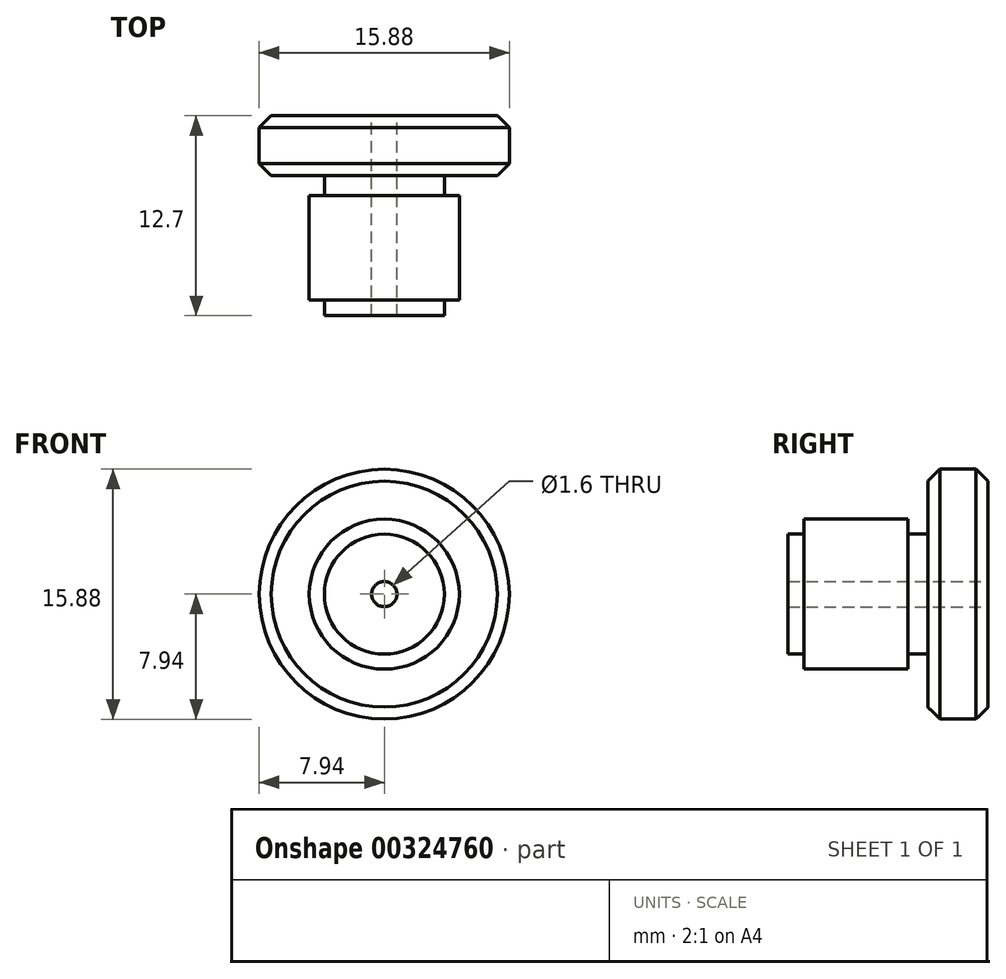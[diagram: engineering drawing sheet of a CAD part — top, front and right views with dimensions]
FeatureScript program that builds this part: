
annotation { "Feature Type Name" : "Feature", "Feature Type Description" : "" }
export const myFeature = defineFeature(function(context is Context, id is Id, definition is map)
    precondition{}
    {
        {
            var Q0;
            Q0=qCreatedBy(makeId("Front.planeOp"),FACE);
            var sketch = newSketch(context, id + "F0", { "sketchPlane" : qUnion([Q0])});
            skCircle(sketch, "E0", {"center": v(0, 0) * mm, "radius": 7.94 * mm});
            skSolve(sketch);
        }
        {
            var Q0;
            Q0=makeQuery(id+"F0.imprint","IMPRINT",FACE,{"disambiguationData":[TD([[makeQuery(id+"F0.imprint","IMPRINT",EDGE,{"derivedFrom":sQuery(id+"F0.wireOp",EDGE,"E0")}),1.0]])]});
            extrude(context, id + "F1", {"entities" : qUnion([Q0]), "depth" : 3.8 * mm, "offsetDistance" : 25.4 * mm});
        }
        {
            var Q0;
            Q0=makeQuery(id+"F1.opExtrude","CAP_FACE",FACE,{"disambiguationData":[OSD([sQuery(id+"F0.wireOp",EDGE,"E0")])],"isStart":false});
            var sketch = newSketch(context, id + "F2", { "sketchPlane" : qUnion([Q0])});
            skCircle(sketch, "E1", {"center": v(0, 0) * mm, "radius": 4.76 * mm});
            skSolve(sketch);
        }
        {
            var Q0;
            Q0=makeQuery(id+"F2.imprint","IMPRINT",FACE,{"disambiguationData":[TD([[makeQuery(id+"F2.imprint","IMPRINT",EDGE,{"derivedFrom":sQuery(id+"F2.wireOp",EDGE,"E1")}),1.0]])]});
            extrude(context, id + "F3", {"entities" : qUnion([Q0]), "operationType" : NewBodyOperationType.ADD, "depth" : 8.9 * mm, "offsetDistance" : 25.4 * mm});
        }
        {
            var Q0;
            Q0=qCreatedBy(makeId("Right.planeOp"),FACE);
            var sketch = newSketch(context, id + "F4", { "sketchPlane" : qUnion([Q0])});
            skLineSegment(sketch, "E2.bottom", {"start": v(-3.81, 3.81) * mm, "end": v(-5.08, 3.81) * mm});
            skLineSegment(sketch, "E2.top", {"start": v(-3.81, 5.97) * mm, "end": v(-5.08, 5.97) * mm});
            skLineSegment(sketch, "E2.left", {"start": v(-3.81, 3.81) * mm, "end": v(-3.81, 5.97) * mm});
            skLineSegment(sketch, "E2.right", {"start": v(-5.08, 3.81) * mm, "end": v(-5.08, 5.97) * mm});
            skSolve(sketch);
        }
        {
            var Q0;
            Q0=makeQuery(id+"F4.imprint","IMPRINT",FACE,{"disambiguationData":[TD([[makeQuery(id+"F4.imprint","IMPRINT",EDGE,{"derivedFrom":sQuery(id+"F4.wireOp",EDGE,"E2.bottom")}),-1.0]])]});
            var Q1;
            Q1=makeQuery(id+"F1.opExtrude","CAP_EDGE",EDGE,{"disambiguationData":[OSD([sQuery(id+"F0.wireOp",EDGE,"E0")])],"isStart":false});
            sweep(context, id + "F5", {"operationType" : NewBodyOperationType.REMOVE, "profiles" : qUnion([Q0]), "path" : qUnion([Q1])});
        }
        {
            var Q0;
            Q0=qCreatedBy(makeId("Right.planeOp"),FACE);
            var sketch = newSketch(context, id + "F6", { "sketchPlane" : qUnion([Q0])});
            skLineSegment(sketch, "E3.bottom", {"start": v(-13.73, 6.97) * mm, "end": v(-11.7, 6.97) * mm});
            skLineSegment(sketch, "E3.top", {"start": v(-13.73, 3.81) * mm, "end": v(-11.7, 3.81) * mm});
            skLineSegment(sketch, "E3.left", {"start": v(-13.73, 6.97) * mm, "end": v(-13.73, 3.81) * mm});
            skLineSegment(sketch, "E3.right", {"start": v(-11.7, 6.97) * mm, "end": v(-11.7, 3.81) * mm});
            skSolve(sketch);
        }
        {
            var Q0;
            Q0=makeQuery(id+"F6.imprint","IMPRINT",FACE,{"disambiguationData":[TD([[makeQuery(id+"F6.imprint","IMPRINT",EDGE,{"derivedFrom":sQuery(id+"F6.wireOp",EDGE,"E3.bottom")}),-1.0]])]});
            var Q1;
            Q1=makeQuery(id+"F3.opExtrude","CAP_EDGE",EDGE,{"disambiguationData":[OSD([sQuery(id+"F2.wireOp",EDGE,"E1")])],"isStart":false});
            sweep(context, id + "F7", {"operationType" : NewBodyOperationType.REMOVE, "profiles" : qUnion([Q0]), "path" : qUnion([Q1])});
        }
        {
            var Q0;
            Q0=makeQuery(id+"F1.opExtrude","CAP_EDGE",EDGE,{"disambiguationData":[OSD([sQuery(id+"F0.wireOp",EDGE,"E0")])],"isStart":true});
            var Q1;
            Q1=makeQuery(id+"F1.opExtrude","CAP_EDGE",EDGE,{"disambiguationData":[OSD([sQuery(id+"F0.wireOp",EDGE,"E0")])],"isStart":false});
            chamfer(context, id + "F8", {"entities" : qUnion([Q0, Q1]), "width" : 0.76 * mm, "tangentPropagation" : true});
        }
        {
            var Q0;
            Q0=makeQuery(id+"F1.opExtrude","CAP_FACE",FACE,{"disambiguationData":[OSD([sQuery(id+"F0.wireOp",EDGE,"E0")])],"isStart":true});
            var sketch = newSketch(context, id + "F9", { "sketchPlane" : qUnion([Q0])});
            skCircle(sketch, "E4", {"center": v(0, 0) * mm, "radius": 0.8 * mm});
            skSolve(sketch);
        }
        {
            var Q0;
            Q0=makeQuery(id+"F9.imprint","IMPRINT",FACE,{"disambiguationData":[TD([[makeQuery(id+"F9.imprint","IMPRINT",EDGE,{"derivedFrom":sQuery(id+"F9.wireOp",EDGE,"E4")}),1.0]])]});
            extrude(context, id + "F10", {"entities" : qUnion([Q0]), "operationType" : NewBodyOperationType.REMOVE, "endBound" : BoundingType.THROUGH_ALL, "oppositeDirection" : true, "depth" : 25.4 * mm, "offsetDistance" : 25.4 * mm});
        }
    });
